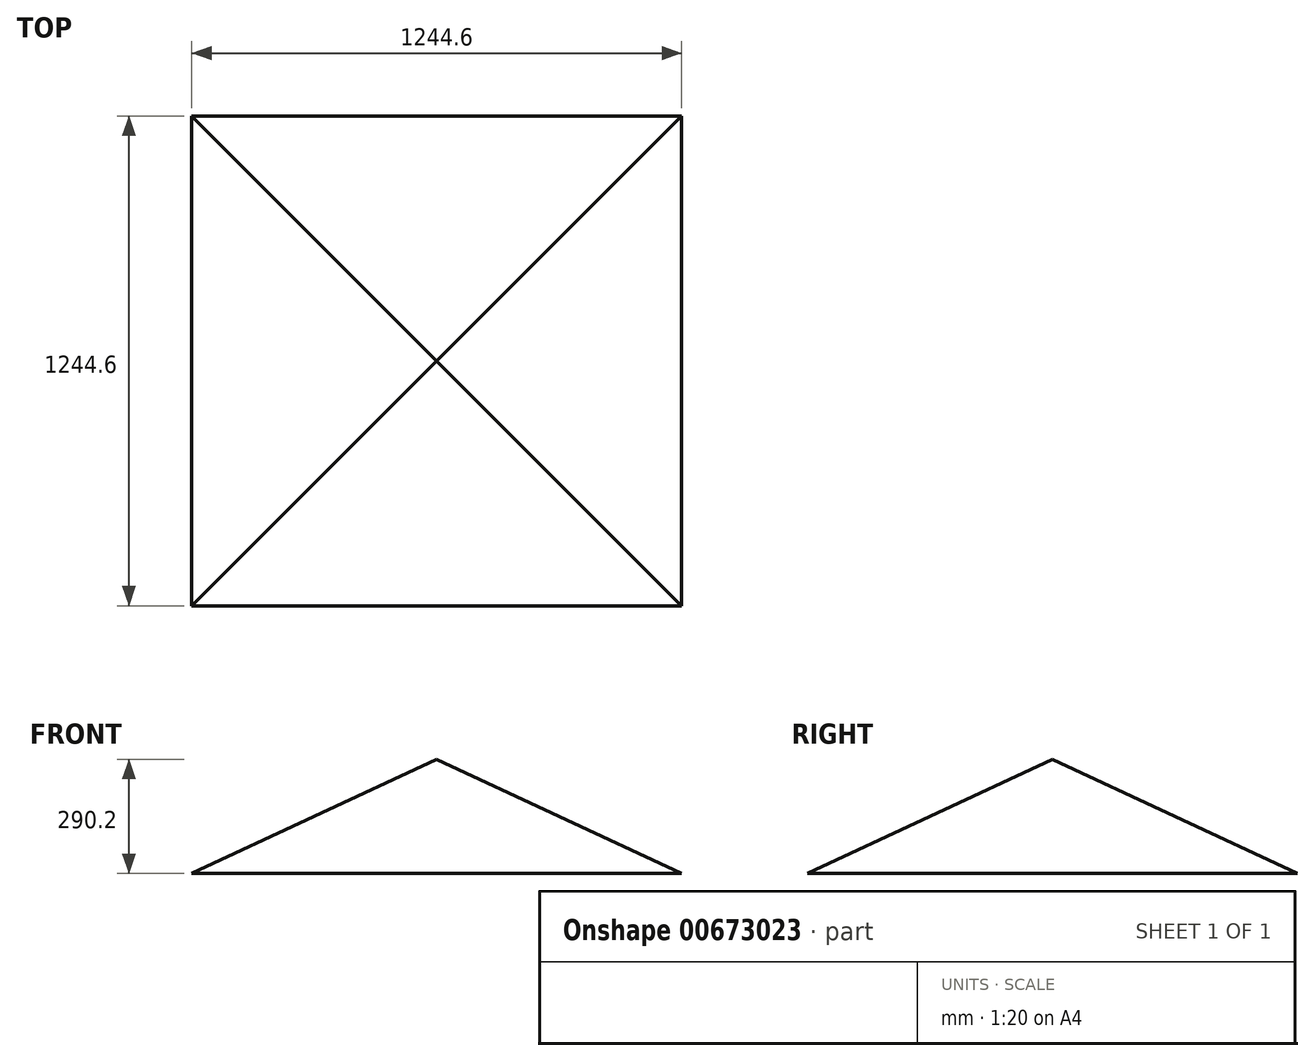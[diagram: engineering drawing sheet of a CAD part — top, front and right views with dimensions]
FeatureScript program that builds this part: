
annotation { "Feature Type Name" : "Feature", "Feature Type Description" : "" }
export const myFeature = defineFeature(function(context is Context, id is Id, definition is map)
    precondition{}
    {
        {
            var Q0;
            Q0=qCreatedBy(makeId("Top.planeOp"),FACE);
            var sketch = newSketch(context, id + "F0", { "sketchPlane" : qUnion([Q0])});
            skLineSegment(sketch, "E0.bottom", {"start": v(-622.3, 622.3) * mm, "end": v(622.3, 622.3) * mm});
            skLineSegment(sketch, "E0.top", {"start": v(-622.3, -622.3) * mm, "end": v(622.3, -622.3) * mm});
            skLineSegment(sketch, "E0.left", {"start": v(-622.3, 622.3) * mm, "end": v(-622.3, -622.3) * mm});
            skLineSegment(sketch, "E0.right", {"start": v(622.3, 622.3) * mm, "end": v(622.3, -622.3) * mm});
            skPoint(sketch, "E0.middle", {"position": v(0, 0) * mm});
            skSolve(sketch);
        }
        {
            var Q0;
            Q0=makeQuery(id+"F0.imprint","IMPRINT",FACE,{"disambiguationData":[TD([[makeQuery(id+"F0.imprint","IMPRINT",EDGE,{"derivedFrom":sQuery(id+"F0.wireOp",EDGE,"E0.bottom")}),-1.0]])]});
            cPlane(context, id + "F1", {"entities" : qUnion([Q0]), "cplaneType" : CPlaneType.OFFSET, "offset" : 290.2 * mm, "width" : 152.4 * mm, "height" : 152.4 * mm});
        }
        {
            var Q0;
            Q0=qCreatedBy(id+"F1.planeOp",FACE);
            var sketch = newSketch(context, id + "F2", { "sketchPlane" : qUnion([Q0])});
            skPoint(sketch, "E1", {"position": v(0, 0) * mm});
            skSolve(sketch);
        }
        {
            var Q0;
            Q0=makeQuery(id+"F0.imprint","IMPRINT",FACE,{"disambiguationData":[TD([[makeQuery(id+"F0.imprint","IMPRINT",EDGE,{"derivedFrom":sQuery(id+"F0.wireOp",EDGE,"E0.bottom")}),-1.0]])]});
            var Q1;
            Q1=sQuery(id+"F2.wireOp",VERTEX,"E1");
            loft(context, id + "F3", {"sheetProfilesArray" : [{ "sheetProfileEntities" : qUnion([Q0]) }, { "sheetProfileEntities" : qUnion([Q1]) }]});
        }
    });
